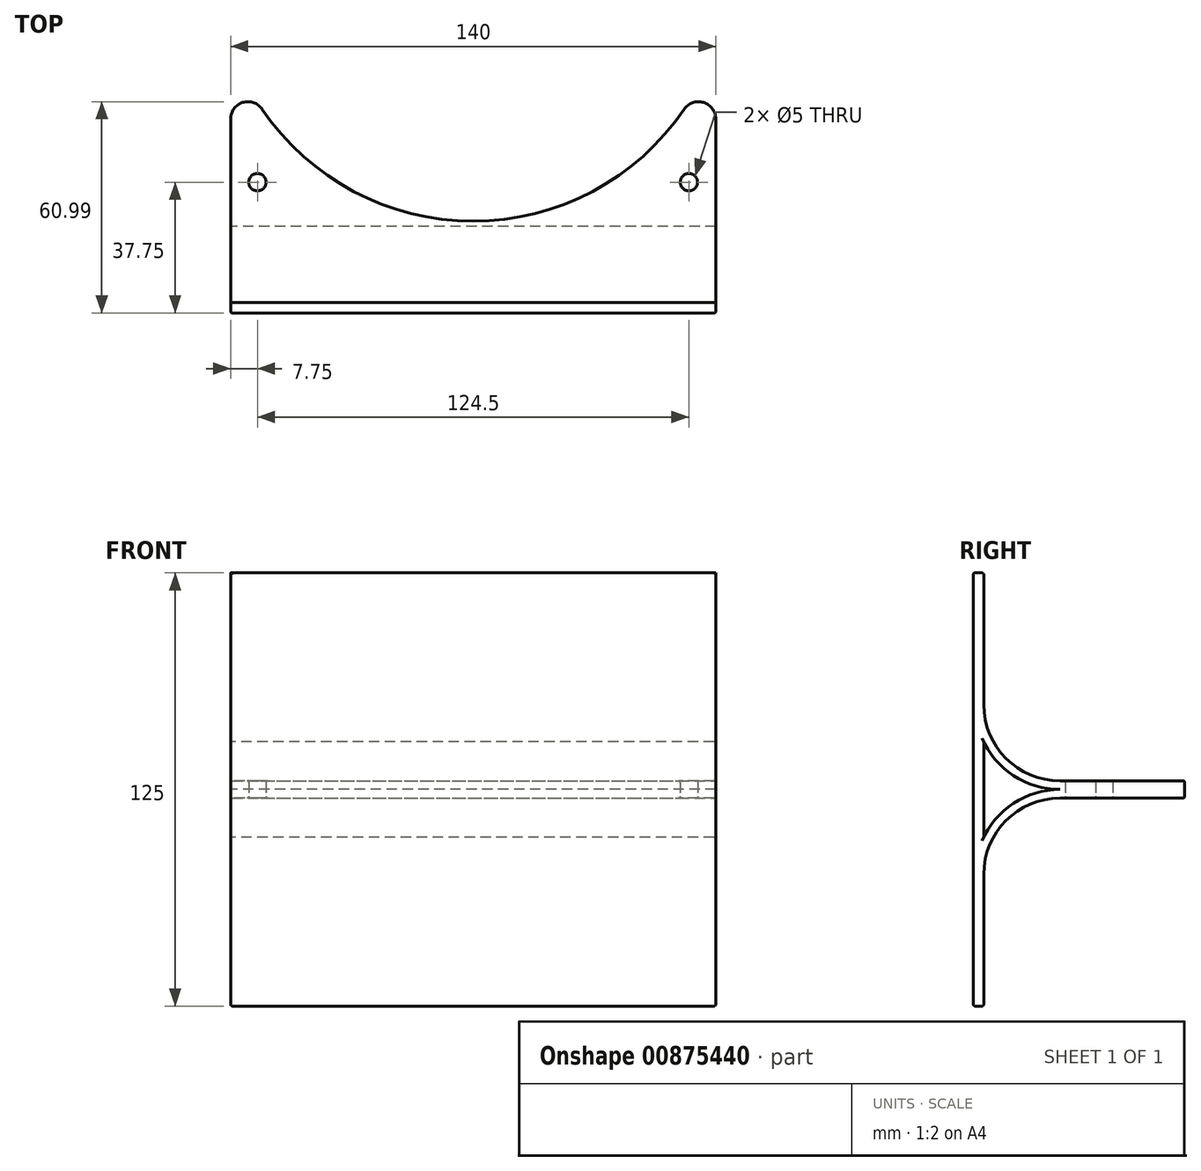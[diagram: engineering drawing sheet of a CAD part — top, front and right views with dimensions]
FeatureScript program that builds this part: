
annotation { "Feature Type Name" : "Feature", "Feature Type Description" : "" }
export const myFeature = defineFeature(function(context is Context, id is Id, definition is map)
    precondition{}
    {
        {
            var Q0;
            Q0=qCreatedBy(makeId("Top.planeOp"),FACE);
            var sketch = newSketch(context, id + "F0", { "sketchPlane" : qUnion([Q0])});
            skArc(sketch, "E0", {"start": v(-70, -22.41) * mm, "mid": v(0, -73.5) * mm, "end": v(70, -22.41) * mm});
            skLineSegment(sketch, "E1", {"start": v(-70, -22.41) * mm, "end": v(-70, -75) * mm});
            skLineSegment(sketch, "E2", {"start": v(-70, -75) * mm, "end": v(70, -75) * mm});
            skLineSegment(sketch, "E3", {"start": v(70, -75) * mm, "end": v(70, -22.41) * mm});
            skCircle(sketch, "E4", {"center": v(62.25, -62.25) * mm, "radius": 2.5 * mm});
            skLineSegment(sketch, "E5", {"start": v(0, 26.99) * mm, "end": v(0, -105.78) * mm, "construction": true});
            skCircle(sketch, "E6.MirrorC", {"center": v(-62.25, -62.25) * mm, "radius": 2.5 * mm});
            skSolve(sketch);
        }
        {
            var Q0;
            Q0 = qSketchRegion(id + "F0", true);
            extrude(context, id + "F1", {"entities" : qUnion([Q0]), "depth" : 5 * mm, "offsetDistance" : 25 * mm});
        }
        {
            var Q0;
            Q0=makeQuery(id+"F1.opExtrude","SWEPT_FACE",FACE,{"disambiguationData":[OSD([sQuery(id+"F0.wireOp",EDGE,"E1")])]});
            var sketch = newSketch(context, id + "F2", { "sketchPlane" : qUnion([Q0])});
            skArc(sketch, "E7", {"start": v(97, -22) * mm, "mid": v(90.56, -6.44) * mm, "end": v(75, 0) * mm});
            skArc(sketch, "E8", {"start": v(75, 5) * mm, "mid": v(90.56, 11.44) * mm, "end": v(97, 27) * mm});
            skLineSegment(sketch, "E9.bottom", {"start": v(97, -60) * mm, "end": v(100, -60) * mm});
            skLineSegment(sketch, "E9.top", {"start": v(97, 65) * mm, "end": v(100, 65) * mm});
            skLineSegment(sketch, "E9.left", {"start": v(97, -60) * mm, "end": v(97, -22) * mm});
            skLineSegment(sketch, "E9.right", {"start": v(100, -60) * mm, "end": v(100, 65) * mm});
            skArc(sketch, "E10", {"start": v(97, -11.22) * mm, "mid": v(87.96, -1.21) * mm, "end": v(75, 2.5) * mm});
            skArc(sketch, "E11", {"start": v(75, 2.5) * mm, "mid": v(87.96, 6.21) * mm, "end": v(97, 16.22) * mm});
            skLineSegment(sketch, "E12", {"start": v(75, 0) * mm, "end": v(75, 2.5) * mm});
            skLineSegment(sketch, "E13", {"start": v(75, 2.5) * mm, "end": v(75, 5) * mm});
            skLineSegment(sketch, "E14.trimOffspring", {"start": v(97, -11.22) * mm, "end": v(97, 16.22) * mm});
            skLineSegment(sketch, "E15.trimOffspring", {"start": v(97, 27) * mm, "end": v(97, 65) * mm});
            skSolve(sketch);
        }
        {
            var Q0;
            Q0 = qSketchRegion(id + "F2", true);
            var Q1;
            Q1=makeQuery(id+"F1.opExtrude","SWEPT_FACE",FACE,{"disambiguationData":[OSD([sQuery(id+"F0.wireOp",EDGE,"E3")])]});
            extrude(context, id + "F3", {"entities" : qUnion([Q0]), "operationType" : NewBodyOperationType.ADD, "endBound" : BoundingType.UP_TO_SURFACE, "oppositeDirection" : true, "depth" : 25 * mm, "endBoundEntityFace" : qUnion([Q1]), "offsetDistance" : 25 * mm});
        }
        {
            var Q0;
            Q0=makeQuery(id+"F2.imprint","IMPRINT",FACE,{"disambiguationData":[TD([[makeQuery(id+"F2.imprint","IMPRINT",EDGE,{"derivedFrom":sQuery(id+"F2.wireOp",EDGE,"E10")}),-1.0]])]});
            extrude(context, id + "F4", {"entities" : qUnion([Q0]), "operationType" : NewBodyOperationType.REMOVE, "endBound" : BoundingType.THROUGH_ALL, "oppositeDirection" : true, "depth" : 25 * mm, "offsetDistance" : 25 * mm});
        }
        {
            var Q0;
            Q0=makeQuery(id+"F1.opExtrude","SWEPT_EDGE",EDGE,{"disambiguationData":[OSD([sQuery(id+"F0.wireOp",EDGE,"E0"),sQuery(id+"F0.wireOp",EDGE,"E3")])]});
            var Q1;
            Q1=makeQuery(id+"F1.opExtrude","SWEPT_EDGE",EDGE,{"disambiguationData":[OSD([sQuery(id+"F0.wireOp",EDGE,"E0"),sQuery(id+"F0.wireOp",EDGE,"E1")])]});
            fillet(context, id + "F5", {"entities" : qUnion([Q0, Q1]), "radius" : 5 * mm, "tangentPropagation" : true, "allowEdgeOverflow" : false});
        }
        {
            var Q0;
            Q0=makeQuery(id+"F1.opExtrude","CAP_EDGE",EDGE,{"disambiguationData":[OSD([sQuery(id+"F0.wireOp",EDGE,"E0")])],"isStart":true});
            var Q1;
            Q1=makeQuery(id+"F3.opExtrude","SWEPT_FACE",FACE,{"disambiguationData":[OSD([sQuery(id+"F2.wireOp",EDGE,"E9.bottom")])]});
            var Q2;
            Q2=makeQuery(id+"F4.boolean.opBoolean","COPY",EDGE,{"derivedFrom":makeQuery(id+"F4.opExtrude","CAP_EDGE",EDGE,{"disambiguationData":[OSD([sQuery(id+"F2.wireOp",EDGE,"E14.trimOffspring")])],"isStart":true})});
            var Q3;
            Q3=makeQuery(id+"F3.opExtrude","SWEPT_FACE",FACE,{"disambiguationData":[OSD([sQuery(id+"F2.wireOp",EDGE,"E8")])]});
            var Q4;
            Q4=makeQuery(id+"F3.opExtrude","SWEPT_FACE",FACE,{"disambiguationData":[OSD([sQuery(id+"F2.wireOp",EDGE,"E15.trimOffspring")])]});
            var Q5;
            Q5=makeQuery(id+"F4.boolean.opBoolean","INTERSECT",EDGE,{"derivedFrom":[makeQuery(id+"F3.boolean.opBoolean","MERGE",FACE,{"derivedFrom":[makeQuery(id+"F1.opExtrude","SWEPT_FACE",FACE,{"disambiguationData":[OSD([sQuery(id+"F0.wireOp",EDGE,"E3")])]}),makeQuery(id+"F3.opExtrude","CAP_FACE",FACE,{"disambiguationData":[OSD([sQuery(id+"F2.wireOp",EDGE,"E7"),sQuery(id+"F2.wireOp",EDGE,"E8"),sQuery(id+"F2.wireOp",EDGE,"E9.bottom"),sQuery(id+"F2.wireOp",EDGE,"E9.top"),sQuery(id+"F2.wireOp",EDGE,"E9.left"),sQuery(id+"F2.wireOp",EDGE,"E9.right"),sQuery(id+"F2.wireOp",EDGE,"E12"),sQuery(id+"F2.wireOp",EDGE,"E13"),sQuery(id+"F2.wireOp",EDGE,"E15.trimOffspring")])],"isStart":false})]}),makeQuery(id+"F4.opExtrude","SWEPT_FACE",FACE,{"disambiguationData":[OSD([sQuery(id+"F2.wireOp",EDGE,"E14.trimOffspring")])]})]});
            var Q6;
            Q6=makeQuery(id+"F3.opExtrude","CAP_EDGE",EDGE,{"disambiguationData":[OSD([sQuery(id+"F2.wireOp",EDGE,"E9.right")])],"isStart":false});
            var Q7;
            Q7=makeQuery(id+"F3.opExtrude","SWEPT_EDGE",EDGE,{"disambiguationData":[OSD([sQuery(id+"F2.wireOp",EDGE,"E9.top"),sQuery(id+"F2.wireOp",EDGE,"E9.right")])]});
            var Q8;
            Q8=makeQuery(id+"F3.opExtrude","CAP_EDGE",EDGE,{"disambiguationData":[OSD([sQuery(id+"F2.wireOp",EDGE,"E9.right")])],"isStart":true});
            var Q9;
            Q9=makeQuery(id+"F1.opExtrude","SWEPT_FACE",FACE,{"disambiguationData":[OSD([sQuery(id+"F0.wireOp",EDGE,"E4")])]});
            var Q10;
            Q10=makeQuery(id+"F1.opExtrude","SWEPT_FACE",FACE,{"disambiguationData":[OSD([sQuery(id+"F0.wireOp",EDGE,"E6.MirrorC")])]});
            fillet(context, id + "F6", {"entities" : qUnion([Q0, Q1, Q2, Q3, Q4, Q5, Q6, Q7, Q8, Q9, Q10]), "radius" : .5 * mm, "tangentPropagation" : true, "allowEdgeOverflow" : false});
        }
    });
